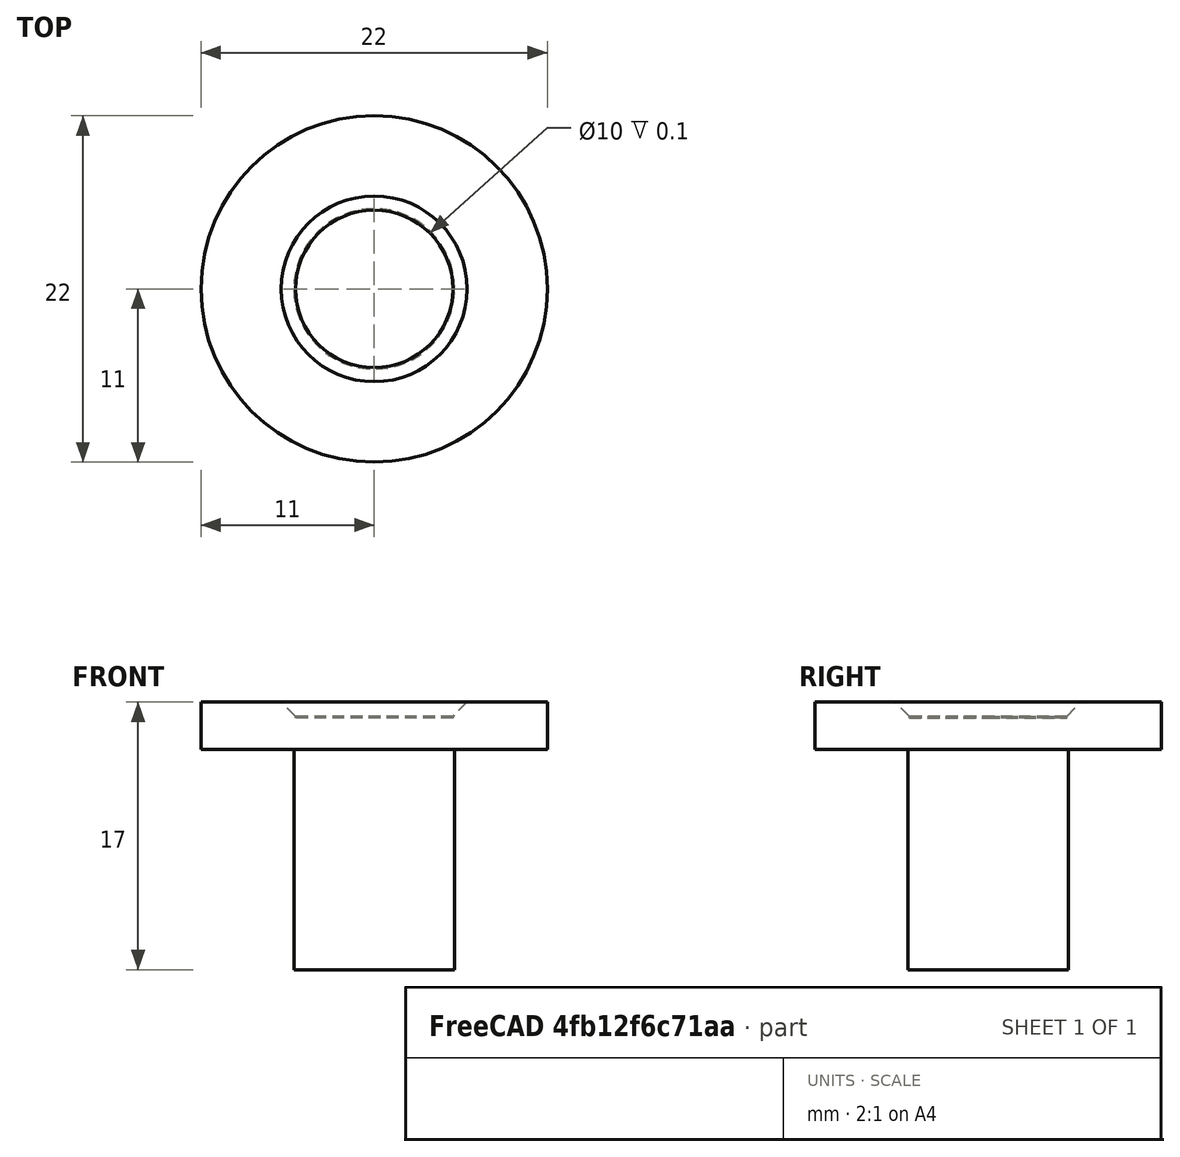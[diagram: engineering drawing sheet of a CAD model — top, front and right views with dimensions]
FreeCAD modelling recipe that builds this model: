
FCSTD DOCUMENT  (FreeCAD 0.20R29603 (Git))
Label: Estampo1Femea
License: All rights reserved
LicenseURL: http://en.wikipedia.org/wiki/All_rights_reserved
objects: TechDraw::DrawViewDimension×7, Sketcher::SketchObject×3, TechDraw::DrawProjGroupItem×3, PartDesign::Pad×2, PartDesign::Pocket×1, PartDesign::Chamfer×1, PartDesign::Body×1, TechDraw::DrawSVGTemplate×1, TechDraw::DrawViewDetail×1, TechDraw::DrawProjGroup×1, TechDraw::DrawViewBalloon×1, TechDraw::DrawViewAnnotation×1, TechDraw::DrawPage×1
note: 12 computed .brp shape members not serialized (recipe doc carries the construction recipe); baked Part::Feature solids carry a one-line shape summary decoded from their .brp

FEATURE [Sketcher::SketchObject] Sketch
  FullyConstrained = true
  MapMode = 5
  Support = -> [XY_Plane]
  sketch-geometry (1):
    g0: Circle CenterX=0 CenterY=0 CenterZ=0 NormalX=0 NormalY=0 NormalZ=1 AngleXU=0 Radius=11
  constraints (2):
    c: Coincident(g0,g-1)
    c: Diameter(g0) = 22
FEATURE [PartDesign::Pad] Pad
  Direction = (0,0,1)
  Length = 3
  Length2 = 10
  Profile = -> Sketch
  ReferenceAxis = -> Sketch [N_Axis]
  Type = 0
FEATURE [Sketcher::SketchObject] Sketch001
  FullyConstrained = true
  MapMode = 5
  Placement = pos=(0,0,3) rot=(0,0,1;0rad)
  Support = -> [Pad]
  sketch-geometry (1):
    g0: Circle CenterX=0 CenterY=0 CenterZ=0 NormalX=0 NormalY=0 NormalZ=1 AngleXU=0 Radius=5
  constraints (2):
    c: Coincident(g0,g-1)
    c: Diameter(g0) = 10
FEATURE [PartDesign::Pocket] Pocket
  BaseFeature = -> Pad
  Direction = (0,0,-1)
  Length = 1
  Length2 = 5
  Profile = -> Sketch001
  ReferenceAxis = -> Sketch001 [N_Axis]
  Type = 0
FEATURE [Sketcher::SketchObject] Sketch002
  FullyConstrained = true
  MapMode = 5
  Placement = pos=(0,0,0) rot=(1,0,0;3.14159rad)
  Support = -> [Pocket]
  sketch-geometry (1):
    g0: Circle CenterX=0 CenterY=0 CenterZ=0 NormalX=0 NormalY=0 NormalZ=1 AngleXU=0 Radius=5.1
  constraints (2):
    c: Coincident(g0,g-1)
    c: Diameter(g0) = 10.2
FEATURE [PartDesign::Pad] Pad001
  BaseFeature = -> Pocket
  Direction = (0,0,-1)
  Length = 14
  Length2 = 10
  Profile = -> Sketch002
  ReferenceAxis = -> Sketch002 [N_Axis]
  Type = 0
FEATURE [PartDesign::Chamfer] Chamfer
  Angle = 45
  Base = -> Pad001 [Edge5]
  BaseFeature = -> Pad001
  ChamferType = 0
  FlipDirection = false
  Size = 0.9
  Size2 = 1
  SupportTransform = false
  UseAllEdges = false
FEATURE [PartDesign::Body] Body
  Group = -> [Sketch,Pad,Sketch001,Pocket,Sketch002,Pad001,Chamfer]
  Origin = -> Origin
  Tip = -> Chamfer
FEATURE [TechDraw::DrawSVGTemplate] Template
  EditableTexts = Designed_by_Name=Nilo; Drawing_number==; FC-Date=31/03/2023; FC-SC=1:1; FC-SH=Sheet; FC-Title=Title; Subtitle=Estampo1 - Femea; Weight=?
  Height = 210
  Orientation = 1
  Width = 297
FEATURE [TechDraw::DrawProjGroupItem] ProjItem
  CoarseView = false
  Direction = (-1e-16,0,1)
  Focus = 100
  HardHidden = false
  IsoCount = 0
  IsoHidden = false
  IsoVisible = false
  LockPosition = true
  Perspective = false
  Rotation = 0
  RotationVector = (1,0,0)
  ScaleType = 2
  SeamHidden = false
  SeamVisible = true
  SmoothHidden = false
  SmoothVisible = true
  Source = -> [Body]
  Type = 0
  X = 0
  XDirection = (-1e-16,-1,0)
  Y = 0
FEATURE [TechDraw::DrawProjGroupItem] ProjItem002
  CoarseView = false
  Direction = (-1,1e-16,-1e-16)
  Focus = 100
  HardHidden = true
  IsoCount = 0
  IsoHidden = false
  IsoVisible = false
  LockPosition = false
  Perspective = false
  Rotation = 0
  RotationVector = (1,0,0)
  ScaleType = 2
  SeamHidden = false
  SeamVisible = true
  SmoothHidden = false
  SmoothVisible = true
  Source = -> [Body]
  Type = 5
  X = 0
  XDirection = (-1e-16,-1,0)
  Y = -48.4052
FEATURE [TechDraw::DrawViewDimension] Dimension
  AngleOverride = false
  Arbitrary = false
  ArbitraryTolerances = false
  EqualTolerance = true
  ExtensionAngle = 0
  FormatSpec = R%.2w
  FormatSpecOverTolerance = %+.2w
  FormatSpecUnderTolerance = %+.2w
  Inverted = false
  LineAngle = 0
  LockPosition = false
  MeasureType = 1
  OverTolerance = 0
  References2D = -> [ProjItem]
  Rotation = 0
  ScaleType = 0
  TheoreticalExact = false
  Type = 4
  UnderTolerance = 0
  X = -21.6748
  Y = -4.37989
FEATURE [TechDraw::DrawViewDimension] Dimension002
  AngleOverride = false
  Arbitrary = false
  ArbitraryTolerances = false
  EqualTolerance = true
  ExtensionAngle = 0
  FormatSpec = R%.2w
  FormatSpecOverTolerance = %+.2w
  FormatSpecUnderTolerance = %+.2w
  Inverted = false
  LineAngle = 0
  LockPosition = false
  MeasureType = 1
  OverTolerance = 0
  References2D = -> [ProjItem]
  Rotation = 0
  ScaleType = 0
  TheoreticalExact = false
  Type = 4
  UnderTolerance = 0
  X = 19.0918
  Y = -6.9629
FEATURE [TechDraw::DrawViewDimension] Dimension004
  AngleOverride = false
  Arbitrary = false
  ArbitraryTolerances = false
  EqualTolerance = true
  ExtensionAngle = 0
  FormatSpec = %.2w
  FormatSpecOverTolerance = %+.2w
  FormatSpecUnderTolerance = %+.2w
  Inverted = false
  LineAngle = 0
  LockPosition = false
  MeasureType = 1
  OverTolerance = 0
  References2D = -> [ProjItem002]
  Rotation = 0
  ScaleType = 0
  TheoreticalExact = false
  Type = 2
  UnderTolerance = 0
  X = 17.801
  Y = 17.0911
FEATURE [TechDraw::DrawViewDetail] Detail  label="det. 1"
  AnchorPoint = (-4.77,7.39,0)
  BaseView = -> ProjItem002
  CoarseView = false
  Direction = (0,1,0)
  Focus = 100
  HardHidden = true
  IsoCount = 0
  IsoHidden = false
  IsoVisible = false
  LockPosition = false
  Perspective = false
  Radius = 3
  Reference = det. 1
  Rotation = 0
  Scale = 3
  ScaleType = 2
  SeamHidden = false
  SeamVisible = true
  SmoothHidden = false
  SmoothVisible = true
  Source = -> [Body]
  X = 175.54
  XDirection = (-1,0,-1e-16)
  Y = 116.626
FEATURE [TechDraw::DrawProjGroupItem] ProjItem003
  CoarseView = false
  Direction = (-0.57735,0.57735,0.57735)
  Focus = 100
  HardHidden = false
  IsoCount = 0
  IsoHidden = false
  IsoVisible = false
  LockPosition = false
  Perspective = false
  Rotation = 0
  RotationVector = (1,0,0)
  ScaleType = 2
  SeamHidden = false
  SeamVisible = true
  SmoothHidden = false
  SmoothVisible = true
  Source = -> [Body]
  Type = 8
  X = -48.4052
  XDirection = (-1e-16,-0.707107,0.707107)
  Y = -48.4052
FEATURE [TechDraw::DrawProjGroup] ProjGroup
  Anchor = -> ProjItem
  AutoDistribute = true
  LockPosition = false
  ProjectionType = 1
  Rotation = 0
  ScaleType = 0
  Source = -> [Body]
  Views = -> [ProjItem,ProjItem002,ProjItem003]
  X = 104.926
  Y = 168.214
  spacingX = 25
  spacingY = 25
FEATURE [TechDraw::DrawViewDimension] Dimension006
  AngleOverride = false
  Arbitrary = false
  ArbitraryTolerances = false
  EqualTolerance = true
  ExtensionAngle = 0
  FormatSpec = ⌀%.2w
  FormatSpecOverTolerance = %+.2w
  FormatSpecUnderTolerance = %+.2w
  Inverted = false
  LineAngle = 0
  LockPosition = false
  MeasureType = 1
  OverTolerance = 0
  References2D = -> [ProjItem002]
  Rotation = 0
  ScaleType = 0
  TheoreticalExact = false
  Type = 1
  UnderTolerance = 0
  X = -16.3013
  Y = -20.6222
FEATURE [TechDraw::DrawViewDimension] Dimension009
  AngleOverride = false
  Arbitrary = false
  ArbitraryTolerances = false
  EqualTolerance = true
  ExtensionAngle = 0
  FormatSpec = %.2w
  FormatSpecOverTolerance = %+.2w
  FormatSpecUnderTolerance = %+.2w
  Inverted = false
  LineAngle = 0
  LockPosition = false
  MeasureType = 1
  OverTolerance = 0
  References2D = -> [ProjItem002]
  Rotation = 0
  ScaleType = 0
  TheoreticalExact = false
  Type = 2
  UnderTolerance = 0
  X = -20.5124
  Y = 0.807818
FEATURE [TechDraw::DrawViewDimension] Dimension010
  AngleOverride = false
  Arbitrary = false
  ArbitraryTolerances = false
  EqualTolerance = true
  ExtensionAngle = 0
  FormatSpec = %.2w
  FormatSpecOverTolerance = %+.2w
  FormatSpecUnderTolerance = %+.2w
  Inverted = false
  LineAngle = 0
  LockPosition = false
  MeasureType = 1
  OverTolerance = 0
  References2D = -> [Detail]
  Rotation = 0
  ScaleType = 0
  TheoreticalExact = false
  Type = 2
  UnderTolerance = 0
  X = -24.5315
  Y = -8.07032
FEATURE [TechDraw::DrawViewDimension] Dimension011
  AngleOverride = false
  Arbitrary = false
  ArbitraryTolerances = false
  EqualTolerance = true
  ExtensionAngle = 0
  FormatSpec = %.2w
  FormatSpecOverTolerance = %+.2w
  FormatSpecUnderTolerance = %+.2w
  Inverted = false
  LineAngle = 0
  LockPosition = false
  MeasureType = 1
  OverTolerance = 0
  References2D = -> [Detail]
  Rotation = 0
  ScaleType = 0
  TheoreticalExact = false
  Type = 6
  UnderTolerance = 0
  X = 22.5389
  Y = -8.42286
FEATURE [TechDraw::DrawViewBalloon] Balloon
  BubbleShape = 0
  EndType = 0
  EndTypeScale = 1
  KinkLength = 5
  LockPosition = false
  OriginX = -4.95115
  OriginY = -6.82515
  Rotation = 0
  ScaleType = 0
  ShapeScale = 1
  SourceView = -> ProjItem003
  Text = 1
  TextWrapLen = -1
  X = 29.0795
  Y = -49.3251
FEATURE [TechDraw::DrawViewAnnotation] Annotation
  Font = osifont
  LineSpace = 80
  LockPosition = false
  MaxWidth = -1
  Rotation = 0
  ScaleType = 0
  Text = 1 - Peça em aço AISI 304
  TextSize = 4
  TextStyle = 0
  X = 50.2857
  Y = 51.4286
FEATURE [TechDraw::DrawPage] Page
  KeepUpdated = true
  NextBalloonIndex = 2
  ProjectionType = 0
  Template = -> Template
  Views = -> [ProjGroup,Dimension,Dimension002,Dimension004,Detail,Dimension006,Dimension009,Dimension010,Dimension011,Balloon,Annotation]
